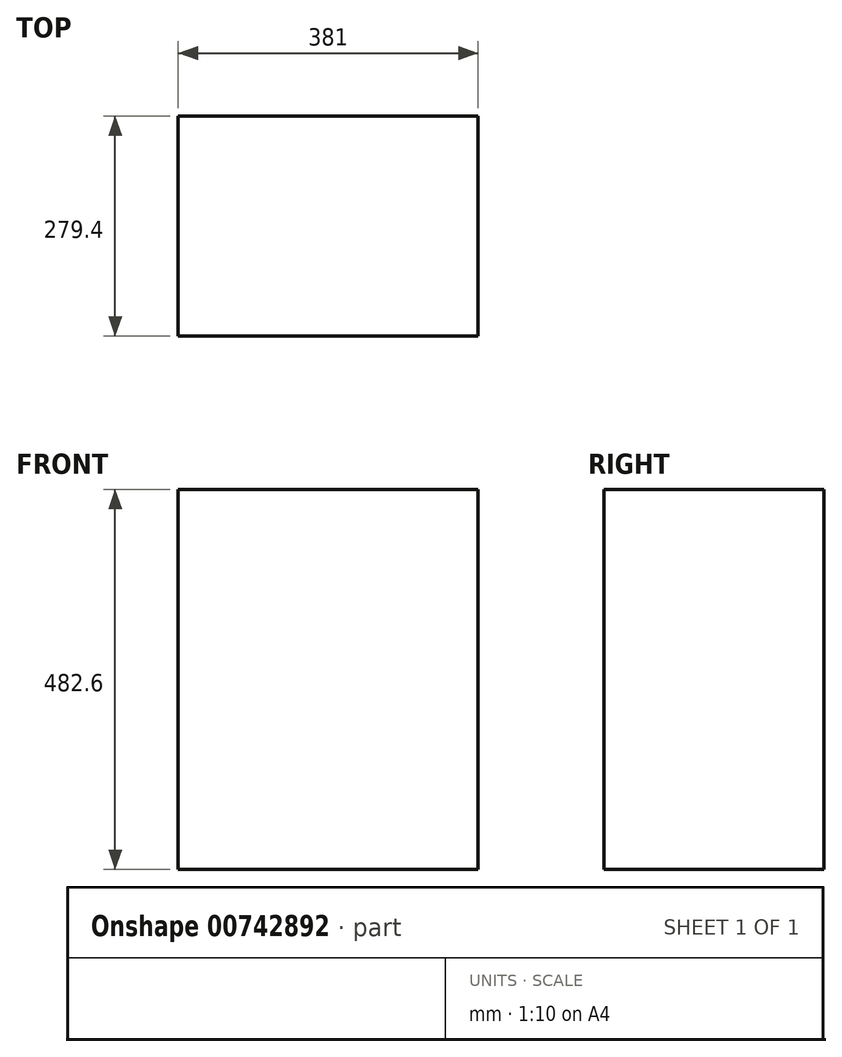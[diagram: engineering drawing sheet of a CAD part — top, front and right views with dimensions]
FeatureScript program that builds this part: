
annotation { "Feature Type Name" : "Feature", "Feature Type Description" : "" }
export const myFeature = defineFeature(function(context is Context, id is Id, definition is map)
    precondition{}
    {
        {
            var Q0;
            Q0=qCreatedBy(makeId("Right.planeOp"),FACE);
            var sketch = newSketch(context, id + "F0", { "sketchPlane" : qUnion([Q0])});
            skLineSegment(sketch, "E0.bottom", {"start": v(-139.7, 241.3) * mm, "end": v(139.7, 241.3) * mm});
            skLineSegment(sketch, "E0.top", {"start": v(-139.7, -241.3) * mm, "end": v(139.7, -241.3) * mm});
            skLineSegment(sketch, "E0.left", {"start": v(-139.7, 241.3) * mm, "end": v(-139.7, -241.3) * mm});
            skLineSegment(sketch, "E0.right", {"start": v(139.7, 241.3) * mm, "end": v(139.7, -241.3) * mm});
            skPoint(sketch, "E0.middle", {"position": v(0, 0) * mm});
            skSolve(sketch);
        }
        {
            var Q0;
            Q0=makeQuery(id+"F0.imprint","IMPRINT",FACE,{"disambiguationData":[TD([[makeQuery(id+"F0.imprint","IMPRINT",EDGE,{"derivedFrom":sQuery(id+"F0.wireOp",EDGE,"E0.bottom")}),-1.0]])]});
            extrude(context, id + "F1", {"entities" : qUnion([Q0]), "depth" : 381 * mm, "offsetDistance" : 25.4 * mm});
        }
    });
